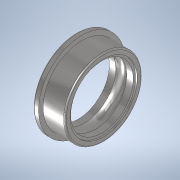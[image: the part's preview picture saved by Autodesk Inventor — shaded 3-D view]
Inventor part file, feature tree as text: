
AUTODESK INVENTOR PART (.ipt)
format: ipt  version: 2020.3 (Build 243373000, 373)  size: 154,112 bytes
history: native  units: mm (DEFAULTED — no unit token found)
features: other x14, revolve x1, sketch x1
ambient origin geometry x8: Origin, YZ Plane, XZ Plane, XY Plane, X Axis, Y Axis, Z Axis, Center Point
bodies: Solid1 (feature_tree)
feature tree (16):
  revolve  "Revolution1"  [1 undecoded]
  other  "ip_st_1_XY"
  other  "ip_st_1_YZ"
  other  "ip_st_1_ZX"
  other  "ip_st_1_X"
  other  "ip_st_1_Y"
  other  "ip_st_1_Z"
  other  "ip_st_1_Center"
  other  "ip_st_2_XY"
  other  "ip_st_2_YZ"
  other  "ip_st_2_ZX"
  other  "ip_st_2_X"
  other  "ip_st_2_Y"
  other  "ip_st_2_Z"
  other  "ip_st_2_Center"
  sketch  "Sketch_1"  dims[d0=360.0deg d1=0.0mm d2=0.0mm]
note: 1 required parameter value undecoded (feature->parameter linkage not recoverable at this tier; creation-order binding heuristic only, values carry confidence <= 0.55)
